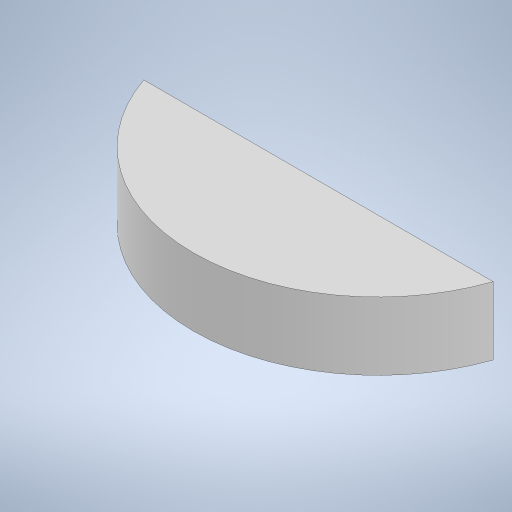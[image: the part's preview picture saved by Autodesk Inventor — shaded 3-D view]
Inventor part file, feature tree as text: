
AUTODESK INVENTOR PART (.ipt)
format: ipt  version: 2024 (Build 280153000, 153)  size: 236,032 bytes
history: native  units: mm
features: sketch x2, other x1, revolve x1, extrude x1
ambient origin geometry x8: Origin, YZ Plane, XZ Plane, XY Plane, X Axis, Y Axis, Z Axis, Center Point
bodies: Body1 (feature_tree)
feature tree (5):
  other  "Sólido1"
  revolve  "Revolución1"  [1 undecoded]
  extrude  "Extrusión1"  Depth=35.0mm
  sketch  "Boceto1"  dims[d0=38.0mm d1=103.4mm]
  sketch  "Boceto2"  dims[d2=3.2mm d3=35.0mm d4=3.4mm d5=3.2mm d6=180.0deg d7=70.0mm d8=100.0mm d9=0.0mm d10=0.5mm d11=0.872665mm]
note: 1 required parameter value undecoded (feature->parameter linkage not recoverable at this tier; creation-order binding heuristic only, values carry confidence <= 0.55)
